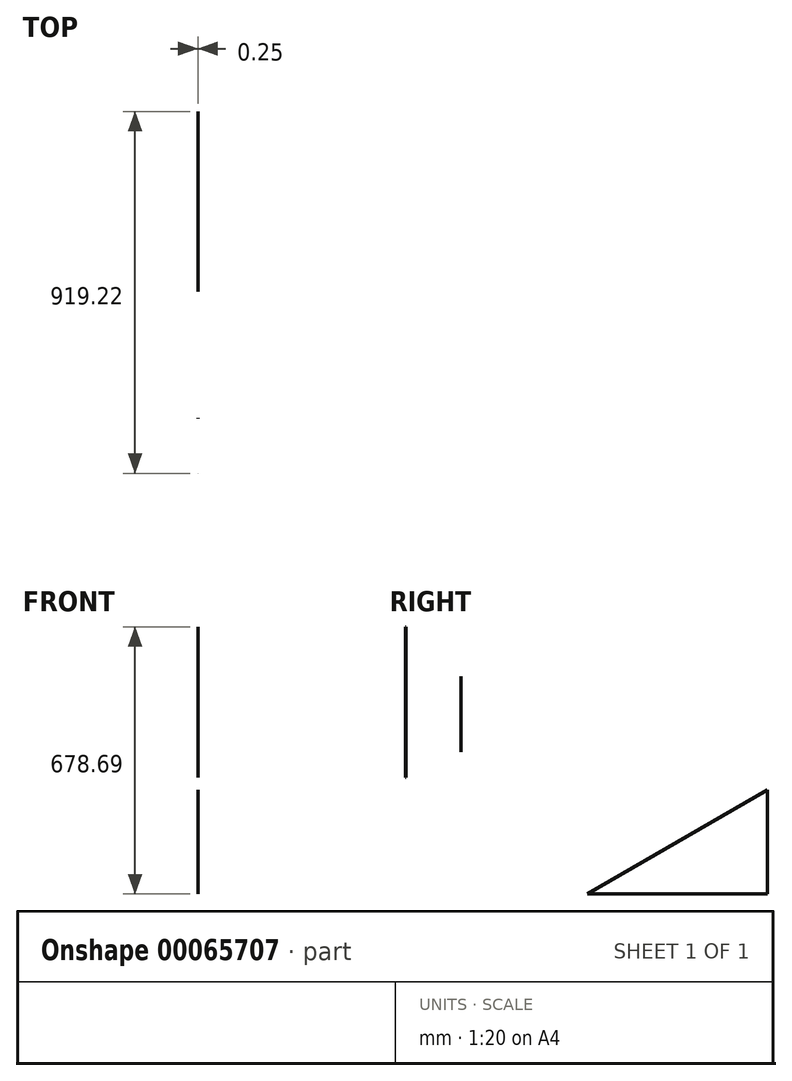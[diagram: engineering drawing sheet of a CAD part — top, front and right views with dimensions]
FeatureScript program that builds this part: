
annotation { "Feature Type Name" : "Feature", "Feature Type Description" : "" }
export const myFeature = defineFeature(function(context is Context, id is Id, definition is map)
    precondition{}
    {
        {
            var Q0;
            Q0=qCreatedBy(makeId("Right.planeOp"),FACE);
            var sketch = newSketch(context, id + "F0", { "sketchPlane" : qUnion([Q0])});
            skLineSegment(sketch, "E0", {"start": v(0, 0) * mm, "end": v(457.2, 263.96) * mm});
            skLineSegment(sketch, "E1", {"start": v(457.2, 263.96) * mm, "end": v(457.2, 0) * mm});
            skLineSegment(sketch, "E2", {"start": v(457.2, 0) * mm, "end": v(0, 0) * mm});
            skSolve(sketch);
        }
        {
            var Q0;
            Q0=makeQuery(id+"F0.imprint","IMPRINT",FACE,{"disambiguationData":[TD([[makeQuery(id+"F0.imprint","IMPRINT",EDGE,{"derivedFrom":sQuery(id+"F0.wireOp",EDGE,"E0")}),-1.0]])]});
            extrude(context, id + "F1", {"entities" : qUnion([Q0]), "depth" : 0.25 * mm});
        }
        {
            var Q0;
            Q0=qCreatedBy(makeId("Right.planeOp"),FACE);
            var sketch = newSketch(context, id + "F2", { "sketchPlane" : qUnion([Q0])});
            skLineSegment(sketch, "E3", {"start": v(-462.02, 295.87) * mm, "end": v(-462.02, 678.7) * mm});
            skLineSegment(sketch, "E4", {"start": v(-462.02, 678.7) * mm, "end": v(-461.76, 678.7) * mm});
            skLineSegment(sketch, "E5", {"start": v(-461.76, 678.7) * mm, "end": v(-461.76, 295.87) * mm});
            skLineSegment(sketch, "E6", {"start": v(-461.76, 295.87) * mm, "end": v(-462.02, 295.87) * mm});
            skLineSegment(sketch, "E7", {"start": v(-461.76, 487.28) * mm, "end": v(-486.45, 487.28) * mm});
            skPoint(sketch, "E7.endSnap0", {"position": v(-461.76, 487.28) * mm});
            skSolve(sketch);
        }
        {
            var Q0;
            Q0 = qSketchRegion(id + "F2", true);
            extrude(context, id + "F3", {"entities" : qUnion([Q0]), "depth" : 0.25 * mm});
        }
        {
            var Q0;
            Q0=qCreatedBy(makeId("Right.planeOp"),FACE);
            var sketch = newSketch(context, id + "F4", { "sketchPlane" : qUnion([Q0])});
            skLineSegment(sketch, "E8.bottom", {"start": v(-322.12, 552.73) * mm, "end": v(-321.87, 552.73) * mm});
            skLineSegment(sketch, "E8.top", {"start": v(-322.12, 361.31) * mm, "end": v(-321.87, 361.31) * mm});
            skLineSegment(sketch, "E8.left", {"start": v(-322.12, 552.73) * mm, "end": v(-322.12, 361.31) * mm});
            skLineSegment(sketch, "E8.right", {"start": v(-321.87, 552.73) * mm, "end": v(-321.87, 361.31) * mm});
            skSolve(sketch);
        }
        {
            var Q0;
            Q0 = qSketchRegion(id + "F4", true);
            extrude(context, id + "F5", {"entities" : qUnion([Q0]), "depth" : 0.25 * mm});
        }
    });
